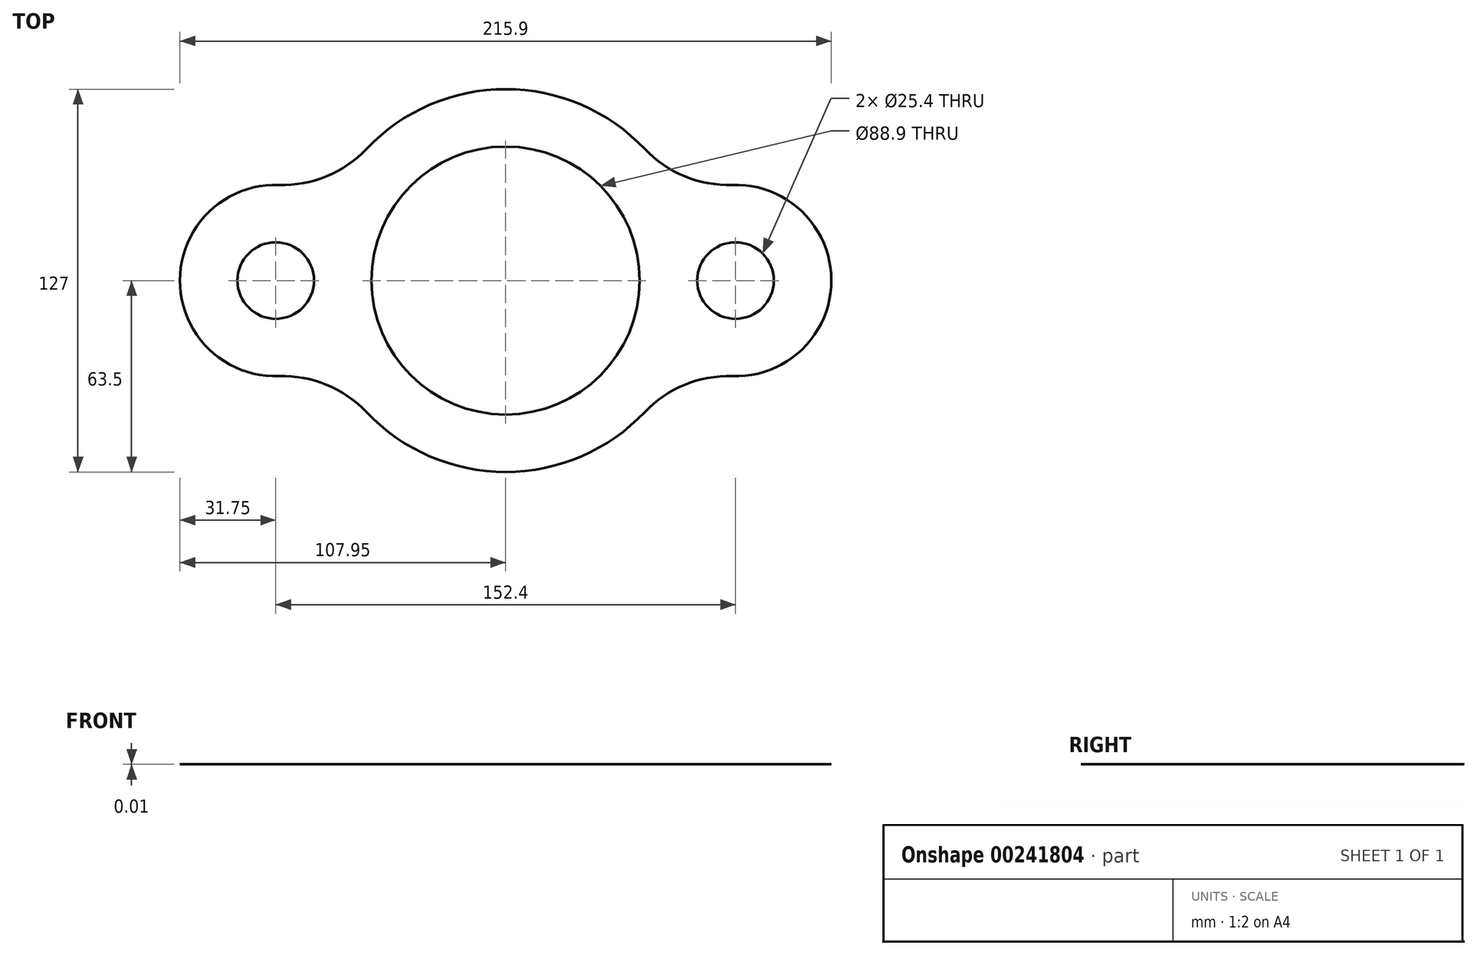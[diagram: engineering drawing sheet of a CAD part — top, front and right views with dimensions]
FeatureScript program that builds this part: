
annotation { "Feature Type Name" : "Feature", "Feature Type Description" : "" }
export const myFeature = defineFeature(function(context is Context, id is Id, definition is map)
    precondition{}
    {
        {
            var Q0;
            Q0=qCreatedBy(makeId("Top.planeOp"),FACE);
            var sketch = newSketch(context, id + "F0", { "sketchPlane" : qUnion([Q0])});
            skCircle(sketch, "E0", {"center": v(0, 0) * mm, "radius": 44.45 * mm});
            skArc(sketch, "E1", {"start": v(-46.14, -43.63) * mm, "mid": v(0, -63.5) * mm, "end": v(46.14, -43.63) * mm});
            skArc(sketch, "E2", {"start": v(-75.12, 31.73) * mm, "mid": v(-107.95, 0) * mm, "end": v(-75.12, -31.73) * mm});
            skCircle(sketch, "E3", {"center": v(-76.2, 0) * mm, "radius": 12.7 * mm});
            skArc(sketch, "E4", {"start": v(75.12, -31.73) * mm, "mid": v(107.95, 0) * mm, "end": v(75.12, 31.73) * mm});
            skCircle(sketch, "E5", {"center": v(76.2, 0) * mm, "radius": 12.7 * mm});
            skArc(sketch, "E6.trimOffspring", {"start": v(46.14, 43.63) * mm, "mid": v(0, 63.5) * mm, "end": v(-46.14, 43.63) * mm});
            skPoint(sketch, "E7.visualSharp", {"position": v(-57.94, 25.98) * mm});
            skArc(sketch, "E7.filletArc", {"start": v(-75.12, 31.73) * mm, "mid": v(-59.35, 34.56) * mm, "end": v(-46.14, 43.63) * mm});
            skPoint(sketch, "E8.visualSharp", {"position": v(-57.94, -25.98) * mm});
            skArc(sketch, "E8.filletArc", {"start": v(-46.14, -43.63) * mm, "mid": v(-59.35, -34.56) * mm, "end": v(-75.12, -31.73) * mm});
            skPoint(sketch, "E9.visualSharp", {"position": v(57.94, -25.98) * mm});
            skArc(sketch, "E9.filletArc", {"start": v(75.12, -31.73) * mm, "mid": v(59.35, -34.56) * mm, "end": v(46.14, -43.63) * mm});
            skPoint(sketch, "E10.visualSharp", {"position": v(57.94, 25.98) * mm});
            skArc(sketch, "E10.filletArc", {"start": v(46.14, 43.63) * mm, "mid": v(59.35, 34.56) * mm, "end": v(75.12, 31.73) * mm});
            skSolve(sketch);
        }
        {
            var Q0;
            Q0=makeQuery(id+"F0.imprint","IMPRINT",FACE,{"disambiguationData":[TD([[makeQuery(id+"F0.imprint","IMPRINT",EDGE,{"derivedFrom":sQuery(id+"F0.wireOp",EDGE,"E0")}),-1.0]])]});
            extrude(context, id + "F1", {"entities" : qUnion([Q0]), "depth" : 1 / 101.6 * mm});
        }
    });
